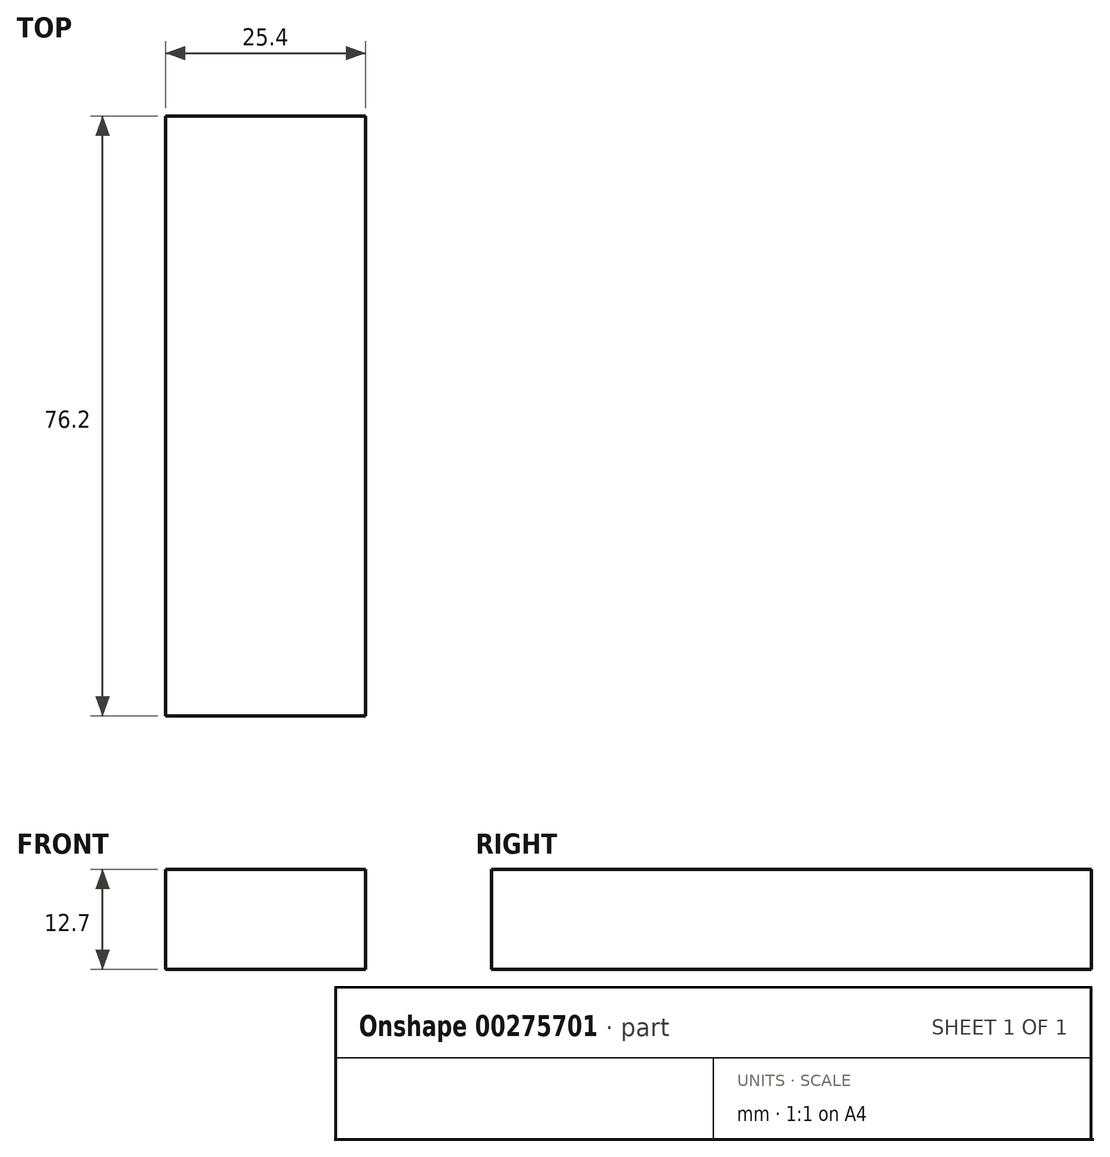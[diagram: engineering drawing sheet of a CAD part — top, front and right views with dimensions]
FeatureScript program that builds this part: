
annotation { "Feature Type Name" : "Feature", "Feature Type Description" : "" }
export const myFeature = defineFeature(function(context is Context, id is Id, definition is map)
    precondition{}
    {
        {
            var Q0;
            Q0=qCreatedBy(makeId("Front.planeOp"),FACE);
            var sketch = newSketch(context, id + "F0", { "sketchPlane" : qUnion([Q0])});
            skLineSegment(sketch, "E0.bottom", {"start": v(-40.55, 26.35) * mm, "end": v(-65.95, 26.35) * mm});
            skLineSegment(sketch, "E0.top", {"start": v(-40.55, 39.05) * mm, "end": v(-65.95, 39.05) * mm});
            skLineSegment(sketch, "E0.left", {"start": v(-40.55, 26.35) * mm, "end": v(-40.55, 39.05) * mm});
            skLineSegment(sketch, "E0.right", {"start": v(-65.95, 26.35) * mm, "end": v(-65.95, 39.05) * mm});
            skPoint(sketch, "E0.middle", {"position": v(-53.25, 32.7) * mm});
            skSolve(sketch);
        }
        {
            var Q0;
            Q0=qSketchRegion(id+"F0",true);
            extrude(context, id + "F1", {"entities" : qUnion([Q0]), "depth" : 76.2 * mm});
        }
    });
